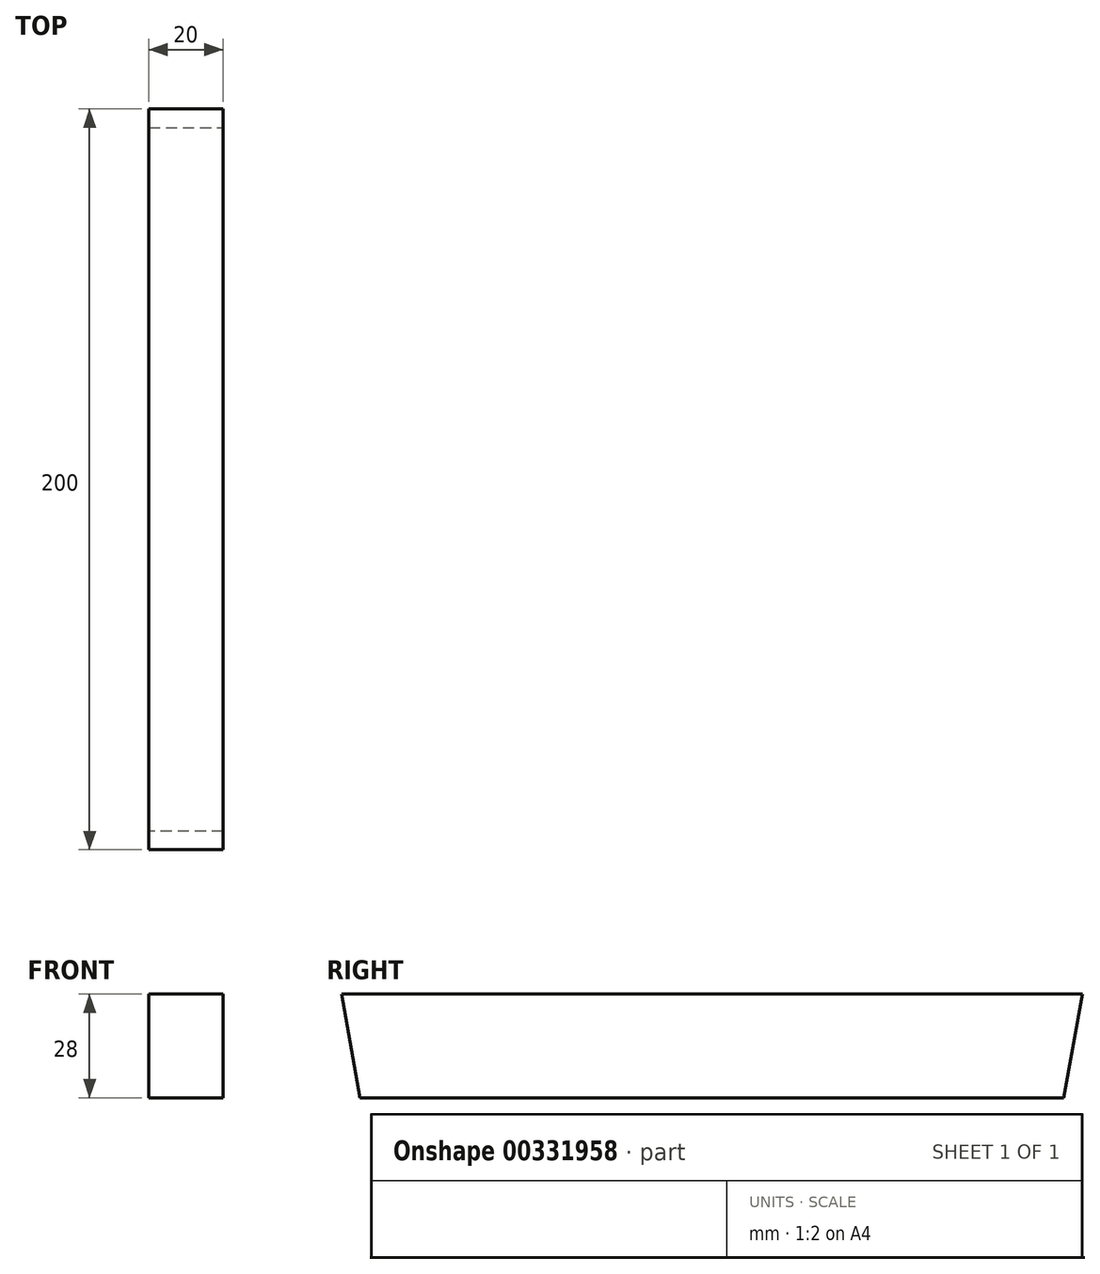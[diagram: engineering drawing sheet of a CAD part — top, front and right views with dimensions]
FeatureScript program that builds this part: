
annotation { "Feature Type Name" : "Feature", "Feature Type Description" : "" }
export const myFeature = defineFeature(function(context is Context, id is Id, definition is map)
    precondition{}
    {
        {
            var Q0;
            Q0=qCreatedBy(makeId("Front.planeOp"),FACE);
            var sketch = newSketch(context, id + "F0", { "sketchPlane" : qUnion([Q0])});
            skLineSegment(sketch, "E0.bottom", {"start": v(10, 14) * mm, "end": v(-10, 14) * mm});
            skLineSegment(sketch, "E0.top", {"start": v(10, -14) * mm, "end": v(-10, -14) * mm});
            skLineSegment(sketch, "E0.left", {"start": v(10, 14) * mm, "end": v(10, -14) * mm});
            skLineSegment(sketch, "E0.right", {"start": v(-10, 14) * mm, "end": v(-10, -14) * mm});
            skPoint(sketch, "E0.middle", {"position": v(0, 0) * mm});
            skSolve(sketch);
        }
        {
            var Q0;
            Q0=makeQuery(id+"F0.imprint","IMPRINT",FACE,{"disambiguationData":[TD([[makeQuery(id+"F0.imprint","IMPRINT",EDGE,{"derivedFrom":sQuery(id+"F0.wireOp",EDGE,"E0.bottom")}),1.0]])]});
            extrude(context, id + "F1", {"entities" : qUnion([Q0]), "depth" : 200 * mm});
        }
        {
            var Q0;
            Q0=makeQuery(id+"F1.opExtrude","CAP_EDGE",EDGE,{"disambiguationData":[OSD([sQuery(id+"F0.wireOp",EDGE,"E0.top")])],"isStart":false});
            chamfer(context, id + "F2", {"entities" : qUnion([Q0]), "chamferType" : ChamferType.TWO_OFFSETS, "width1" : 5 * mm, "oppositeDirection" : false, "width2" : 28 * mm, "tangentPropagation" : true});
        }
        {
            var Q0;
            Q0=makeQuery(id+"F1.opExtrude","CAP_EDGE",EDGE,{"disambiguationData":[OSD([sQuery(id+"F0.wireOp",EDGE,"E0.top")])],"isStart":true});
            chamfer(context, id + "F3", {"entities" : qUnion([Q0]), "chamferType" : ChamferType.TWO_OFFSETS, "width1" : 28 * mm, "oppositeDirection" : false, "width2" : 5 * mm, "tangentPropagation" : true});
        }
    });
